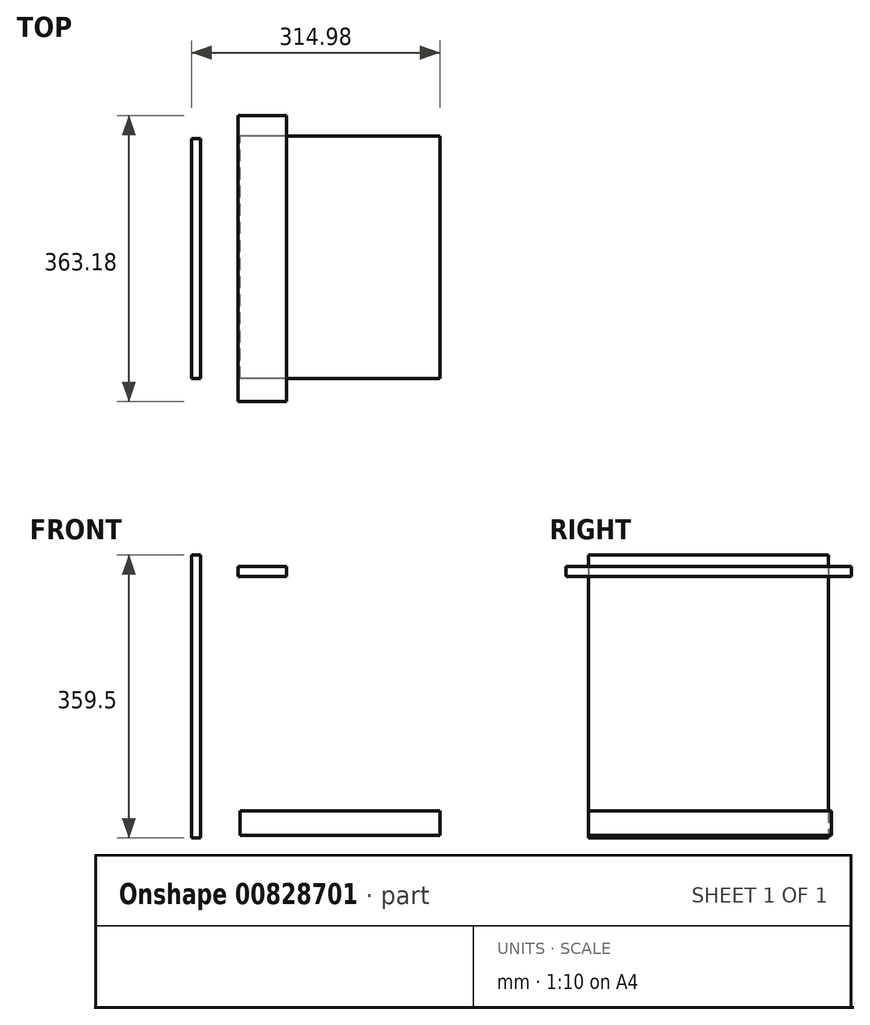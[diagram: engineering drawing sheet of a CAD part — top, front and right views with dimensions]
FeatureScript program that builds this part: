
annotation { "Feature Type Name" : "Feature", "Feature Type Description" : "" }
export const myFeature = defineFeature(function(context is Context, id is Id, definition is map)
    precondition{}
    {
        {
            var Q0;
            Q0=qCreatedBy(makeId("Top.planeOp"),FACE);
            var sketch = newSketch(context, id + "F0", { "sketchPlane" : qUnion([Q0])});
            skLineSegment(sketch, "E0.bottom", {"start": v(59.13, 29.2) * mm, "end": v(-2.18, 29.2) * mm});
            skLineSegment(sketch, "E0.top", {"start": v(59.13, -29.2) * mm, "end": v(-2.18, -29.2) * mm});
            skLineSegment(sketch, "E0.left", {"start": v(59.13, 29.2) * mm, "end": v(59.13, -29.2) * mm});
            skLineSegment(sketch, "E0.right", {"start": v(-2.18, 29.2) * mm, "end": v(-2.18, -29.2) * mm});
            skPoint(sketch, "E0.middle", {"position": v(28.47, 0) * mm});
            skSolve(sketch);
        }
        {
            var Q0;
            Q0=makeQuery(id+"F0.imprint","IMPRINT",FACE,{"disambiguationData":[TD([[makeQuery(id+"F0.imprint","IMPRINT",EDGE,{"derivedFrom":sQuery(id+"F0.wireOp",EDGE,"E0.bottom")}),1.0]])]});
            extrude(context, id + "F1", {"entities" : qUnion([Q0]), "depth" : 13 * mm, "offsetDistance" : 25.4 * mm});
        }
        {
            var Q0;
            Q0=qCreatedBy(makeId("Front.planeOp"),FACE);
            var sketch = newSketch(context, id + "F2", { "sketchPlane" : qUnion([Q0])});
            skLineSegment(sketch, "E1.bottom", {"start": v(-49.89, 27.35) * mm, "end": v(-60.98, 27.35) * mm});
            skLineSegment(sketch, "E1.top", {"start": v(-49.89, -27.35) * mm, "end": v(-60.98, -27.35) * mm});
            skLineSegment(sketch, "E1.left", {"start": v(-49.89, 27.35) * mm, "end": v(-49.89, -27.35) * mm});
            skLineSegment(sketch, "E1.right", {"start": v(-60.98, 27.35) * mm, "end": v(-60.98, -27.35) * mm});
            skPoint(sketch, "E1.middle", {"position": v(-55.43, 0) * mm});
            skSolve(sketch);
        }
        {
            var Q0;
            Q0=makeQuery(id+"F2.imprint","IMPRINT",FACE,{"disambiguationData":[TD([[makeQuery(id+"F2.imprint","IMPRINT",EDGE,{"derivedFrom":sQuery(id+"F2.wireOp",EDGE,"E1.bottom")}),1.0]])]});
            extrude(context, id + "F3", {"entities" : qUnion([Q0]), "depth" : 152.4 * mm, "offsetDistance" : 25.4 * mm});
        }
        {
            var Q0;
            Q0=makeQuery(id+"F3.opExtrude","CAP_FACE",FACE,{"disambiguationData":[OSD([sQuery(id+"F2.wireOp",EDGE,"E1.bottom"),sQuery(id+"F2.wireOp",EDGE,"E1.top"),sQuery(id+"F2.wireOp",EDGE,"E1.left"),sQuery(id+"F2.wireOp",EDGE,"E1.right")])],"isStart":true});
            extrude(context, id + "F4", {"entities" : qUnion([Q0]), "operationType" : NewBodyOperationType.ADD, "depth" : 152.4 * mm, "offsetDistance" : 25.4 * mm});
        }
        {
            var Q0;
            Q0=makeQuery(id+"F1.opExtrude","SWEPT_FACE",FACE,{"disambiguationData":[OSD([sQuery(id+"F0.wireOp",EDGE,"E0.top")])]});
            extrude(context, id + "F5", {"entities" : qUnion([Q0]), "operationType" : NewBodyOperationType.ADD, "depth" : 152.4 * mm, "offsetDistance" : 25.4 * mm});
        }
        {
            var Q0;
            Q0=makeQuery(id+"F1.opExtrude","SWEPT_FACE",FACE,{"disambiguationData":[OSD([sQuery(id+"F0.wireOp",EDGE,"E0.bottom")])]});
            extrude(context, id + "F6", {"entities" : qUnion([Q0]), "operationType" : NewBodyOperationType.ADD, "depth" : 152.4 * mm, "offsetDistance" : 25.4 * mm});
        }
        {
            var Q0;
            {var subQ0=sQuery(id+"F2.wireOp",EDGE,"E1.top");Q0=makeQuery(id+"F4.boolean.opBoolean","MERGE",FACE,{"derivedFrom":[makeQuery(id+"F3.opExtrude","SWEPT_FACE",FACE,{"disambiguationData":[OSD([subQ0])]}),makeQuery(id+"F4.opExtrude","SWEPT_FACE",FACE,{"disambiguationData":[OSD([subQ0])]})]});}
            extrude(context, id + "F7", {"entities" : qUnion([Q0]), "operationType" : NewBodyOperationType.ADD, "depth" : 304.8 * mm, "offsetDistance" : 25.4 * mm});
        }
        {
            var Q0;
            {var subQ0=sQuery(id+"F2.wireOp",EDGE,"E1.left");Q0=makeQuery(id+"F7.boolean.opBoolean","MERGE",FACE,{"derivedFrom":[makeQuery(id+"F4.boolean.opBoolean","MERGE",FACE,{"derivedFrom":[makeQuery(id+"F3.opExtrude","SWEPT_FACE",FACE,{"disambiguationData":[OSD([subQ0])]}),makeQuery(id+"F4.opExtrude","SWEPT_FACE",FACE,{"disambiguationData":[OSD([subQ0])]})]}),makeQuery(id+"F7.opExtrude","SWEPT_FACE",FACE,{"disambiguationData":[OSD([sQuery(id+"F2.wireOp",EDGE,"E1.top"),subQ0])]})]});}
            var sketch = newSketch(context, id + "F8", { "sketchPlane" : qUnion([Q0])});
            skSolve(sketch);
        }
        {
            var Q0;
            Q0=qCreatedBy(makeId("Right.planeOp"),FACE);
            var sketch = newSketch(context, id + "F9", { "sketchPlane" : qUnion([Q0])});
            skLineSegment(sketch, "E2.bottom", {"start": v(-152.5, -297.95) * mm, "end": v(155.68, -297.95) * mm});
            skLineSegment(sketch, "E2.top", {"start": v(-152.5, -328.93) * mm, "end": v(155.68, -328.93) * mm});
            skLineSegment(sketch, "E2.left", {"start": v(-152.5, -297.95) * mm, "end": v(-152.5, -328.93) * mm});
            skLineSegment(sketch, "E2.right", {"start": v(155.68, -297.95) * mm, "end": v(155.68, -328.93) * mm});
            skSolve(sketch);
        }
        {
            var Q0;
            Q0=makeQuery(id+"F9.imprint","IMPRINT",FACE,{"disambiguationData":[TD([[makeQuery(id+"F9.imprint","IMPRINT",EDGE,{"derivedFrom":sQuery(id+"F9.wireOp",EDGE,"E2.bottom")}),-1.0]])]});
            extrude(context, id + "F10", {"entities" : qUnion([Q0]), "depth" : 254 * mm, "offsetDistance" : 25.4 * mm});
        }
    });
